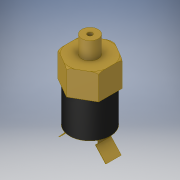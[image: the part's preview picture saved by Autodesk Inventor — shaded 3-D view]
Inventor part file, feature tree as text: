
AUTODESK INVENTOR PART (.ipt)
format: ipt  version: 2018.3 (Build 223284000, 284)  size: 160,256 bytes
history: native  units: in
note: dims shown in document units (in); Inventor stores cm internally (conversion verified against a paired STEP export)
features: mirror x1
ambient origin geometry x8: Origin, YZ Plane, XZ Plane, XY Plane, X Axis, Y Axis, Z Axis, Center Point
bodies: Solid1 (feature_tree)
feature tree (1):
  mirror  "Mirror1"
